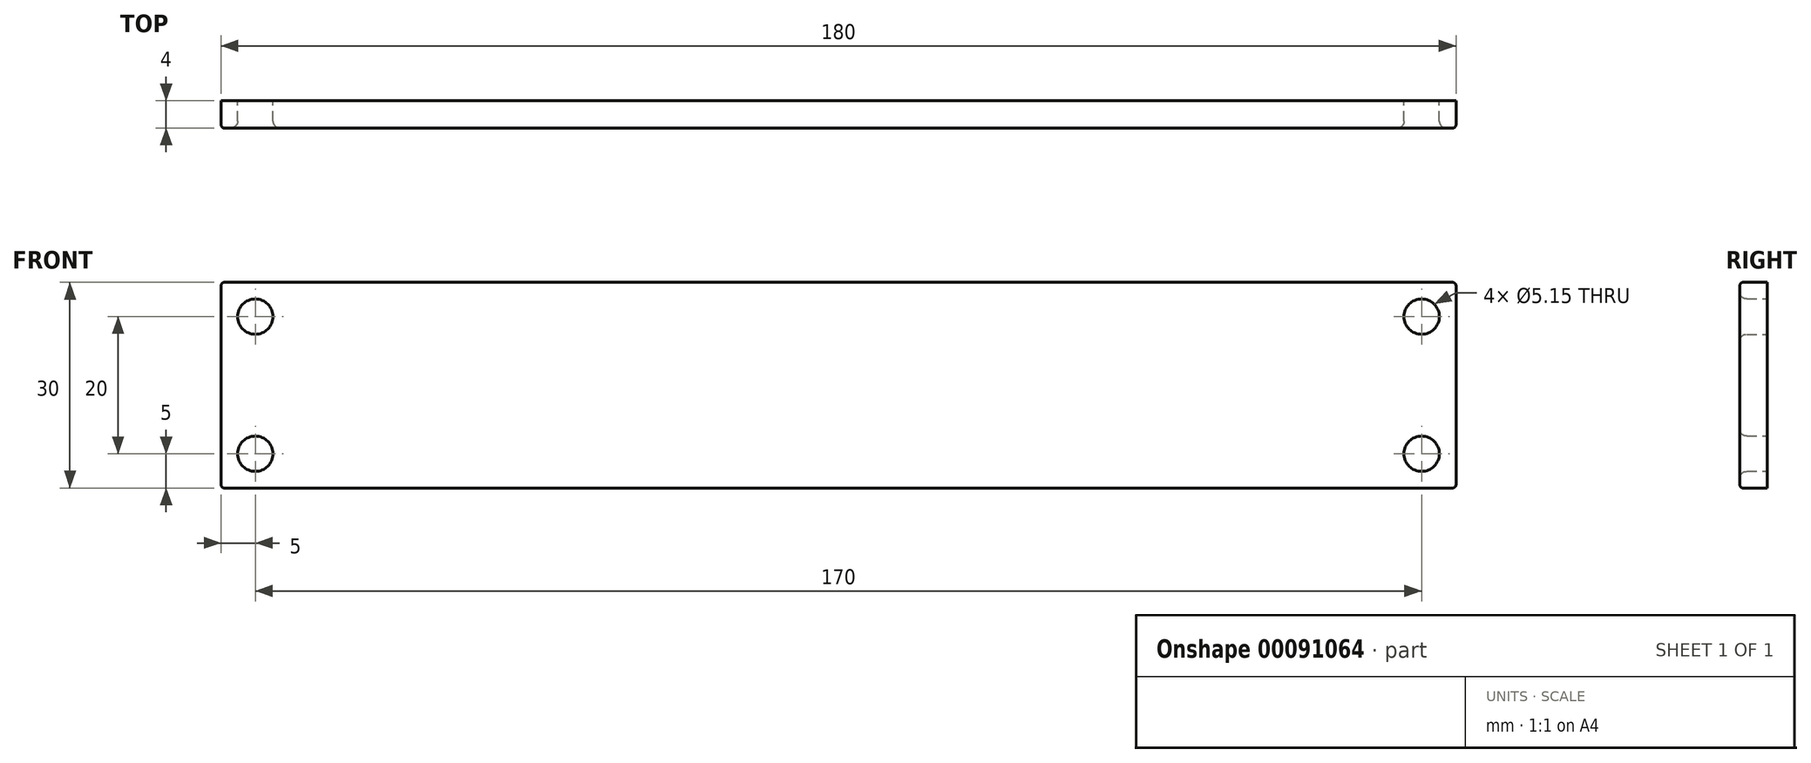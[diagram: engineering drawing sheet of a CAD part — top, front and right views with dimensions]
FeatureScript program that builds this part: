
annotation { "Feature Type Name" : "Feature", "Feature Type Description" : "" }
export const myFeature = defineFeature(function(context is Context, id is Id, definition is map)
    precondition{}
    {
        {
            var Q0;
            Q0=qCreatedBy(makeId("Front.planeOp"),FACE);
            var sketch = newSketch(context, id + "F0", { "sketchPlane" : qUnion([Q0])});
            skLineSegment(sketch, "E0.bottom", {"start": v(-90, -15) * mm, "end": v(90, -15) * mm});
            skLineSegment(sketch, "E0.top", {"start": v(-90, 15) * mm, "end": v(90, 15) * mm});
            skLineSegment(sketch, "E0.left", {"start": v(-90, -15) * mm, "end": v(-90, 15) * mm});
            skLineSegment(sketch, "E0.right", {"start": v(90, -15) * mm, "end": v(90, 15) * mm});
            skPoint(sketch, "E0.middle", {"position": v(0, 0) * mm});
            skCircle(sketch, "E1", {"center": v(-85, 10) * mm, "radius": 2.58 * mm});
            skPoint(sketch, "E2.start.orphan", {"position": v(-90, 0) * mm});
            skPoint(sketch, "E3.orphan", {"position": v(0, 15) * mm});
            skPoint(sketch, "E4.end.orphan", {"position": v(0, -15) * mm});
            skLineSegment(sketch, "E5", {"start": v(-90, 0) * mm, "end": v(0, 0) * mm, "construction": true});
            skLineSegment(sketch, "E6", {"start": v(0, 15) * mm, "end": v(0, -15) * mm, "construction": true});
            skCircle(sketch, "E7.MirrorC", {"center": v(-85, -10) * mm, "radius": 2.58 * mm});
            skCircle(sketch, "E8.MirrorC", {"center": v(85, 10) * mm, "radius": 2.58 * mm});
            skCircle(sketch, "E9.MirrorC", {"center": v(85, -10) * mm, "radius": 2.58 * mm});
            skSolve(sketch);
        }
        {
            var Q0;
            Q0=makeQuery(id+"F0.imprint","IMPRINT",FACE,{"disambiguationData":[TD([[makeQuery(id+"F0.imprint","IMPRINT",EDGE,{"derivedFrom":sQuery(id+"F0.wireOp",EDGE,"E0.bottom")}),1.0]])]});
            extrude(context, id + "F1", {"entities" : qUnion([Q0]), "depth" : 4 * mm});
        }
        {
            var Q0;
            Q0=makeQuery(id+"F1.opExtrude","CAP_EDGE",EDGE,{"disambiguationData":[OSD([sQuery(id+"F0.wireOp",EDGE,"E1")])],"isStart":false});
            var Q1;
            Q1=makeQuery(id+"F1.opExtrude","CAP_EDGE",EDGE,{"disambiguationData":[OSD([sQuery(id+"F0.wireOp",EDGE,"f5b72a5b-8583-449a-bdbf-9ac5a681e1fd0.MirrorC")])],"isStart":false});
            var Q2;
            Q2=makeQuery(id+"F1.opExtrude","CAP_EDGE",EDGE,{"disambiguationData":[OSD([sQuery(id+"F0.wireOp",EDGE,"2623e306-60f4-4522-aa65-1e3e8c2cf5b60.MirrorC")])],"isStart":false});
            var Q3;
            Q3=makeQuery(id+"F1.opExtrude","CAP_EDGE",EDGE,{"disambiguationData":[OSD([sQuery(id+"F0.wireOp",EDGE,"be81a34d-1d50-4ce7-a7a8-4484a1701fac0.MirrorC")])],"isStart":false});
            var Q4;
            Q4=makeQuery(id+"F1.opExtrude","CAP_EDGE",EDGE,{"disambiguationData":[OSD([sQuery(id+"F0.wireOp",EDGE,"E7.MirrorC")])],"isStart":false});
            var Q5;
            Q5=makeQuery(id+"F1.opExtrude","CAP_EDGE",EDGE,{"disambiguationData":[OSD([sQuery(id+"F0.wireOp",EDGE,"E8.MirrorC")])],"isStart":false});
            var Q6;
            Q6=makeQuery(id+"F1.opExtrude","CAP_EDGE",EDGE,{"disambiguationData":[OSD([sQuery(id+"F0.wireOp",EDGE,"E9.MirrorC")])],"isStart":false});
            fillet(context, id + "F2", {"entities" : qUnion([Q0, Q1, Q2, Q3, Q4, Q5, Q6]), "radius" : 1 * mm, "tangentPropagation" : true, "allowEdgeOverflow" : false});
        }
        {
            var Q0;
            Q0=makeQuery(id+"F1.opExtrude","CAP_EDGE",EDGE,{"disambiguationData":[OSD([sQuery(id+"F0.wireOp",EDGE,"E0.top")])],"isStart":false});
            var Q1;
            Q1=makeQuery(id+"F1.opExtrude","CAP_EDGE",EDGE,{"disambiguationData":[OSD([sQuery(id+"F0.wireOp",EDGE,"E0.left")])],"isStart":false});
            var Q2;
            Q2=makeQuery(id+"F1.opExtrude","CAP_EDGE",EDGE,{"disambiguationData":[OSD([sQuery(id+"F0.wireOp",EDGE,"E0.bottom")])],"isStart":false});
            var Q3;
            Q3=makeQuery(id+"F1.opExtrude","CAP_EDGE",EDGE,{"disambiguationData":[OSD([sQuery(id+"F0.wireOp",EDGE,"E0.right")])],"isStart":false});
            var Q4;
            Q4=makeQuery(id+"F1.opExtrude","SWEPT_EDGE",EDGE,{"disambiguationData":[OSD([sQuery(id+"F0.wireOp",EDGE,"E0.top"),sQuery(id+"F0.wireOp",EDGE,"E0.left")])]});
            var Q5;
            Q5=makeQuery(id+"F1.opExtrude","SWEPT_EDGE",EDGE,{"disambiguationData":[OSD([sQuery(id+"F0.wireOp",EDGE,"E0.bottom"),sQuery(id+"F0.wireOp",EDGE,"E0.left")])]});
            var Q6;
            Q6=makeQuery(id+"F1.opExtrude","SWEPT_EDGE",EDGE,{"disambiguationData":[OSD([sQuery(id+"F0.wireOp",EDGE,"E0.top"),sQuery(id+"F0.wireOp",EDGE,"E0.right")])]});
            var Q7;
            Q7=makeQuery(id+"F1.opExtrude","SWEPT_EDGE",EDGE,{"disambiguationData":[OSD([sQuery(id+"F0.wireOp",EDGE,"E0.bottom"),sQuery(id+"F0.wireOp",EDGE,"E0.right")])]});
            fillet(context, id + "F3", {"entities" : qUnion([Q0, Q1, Q2, Q3, Q4, Q5, Q6, Q7]), "radius" : .5 * mm, "tangentPropagation" : true, "allowEdgeOverflow" : false});
        }
    });
